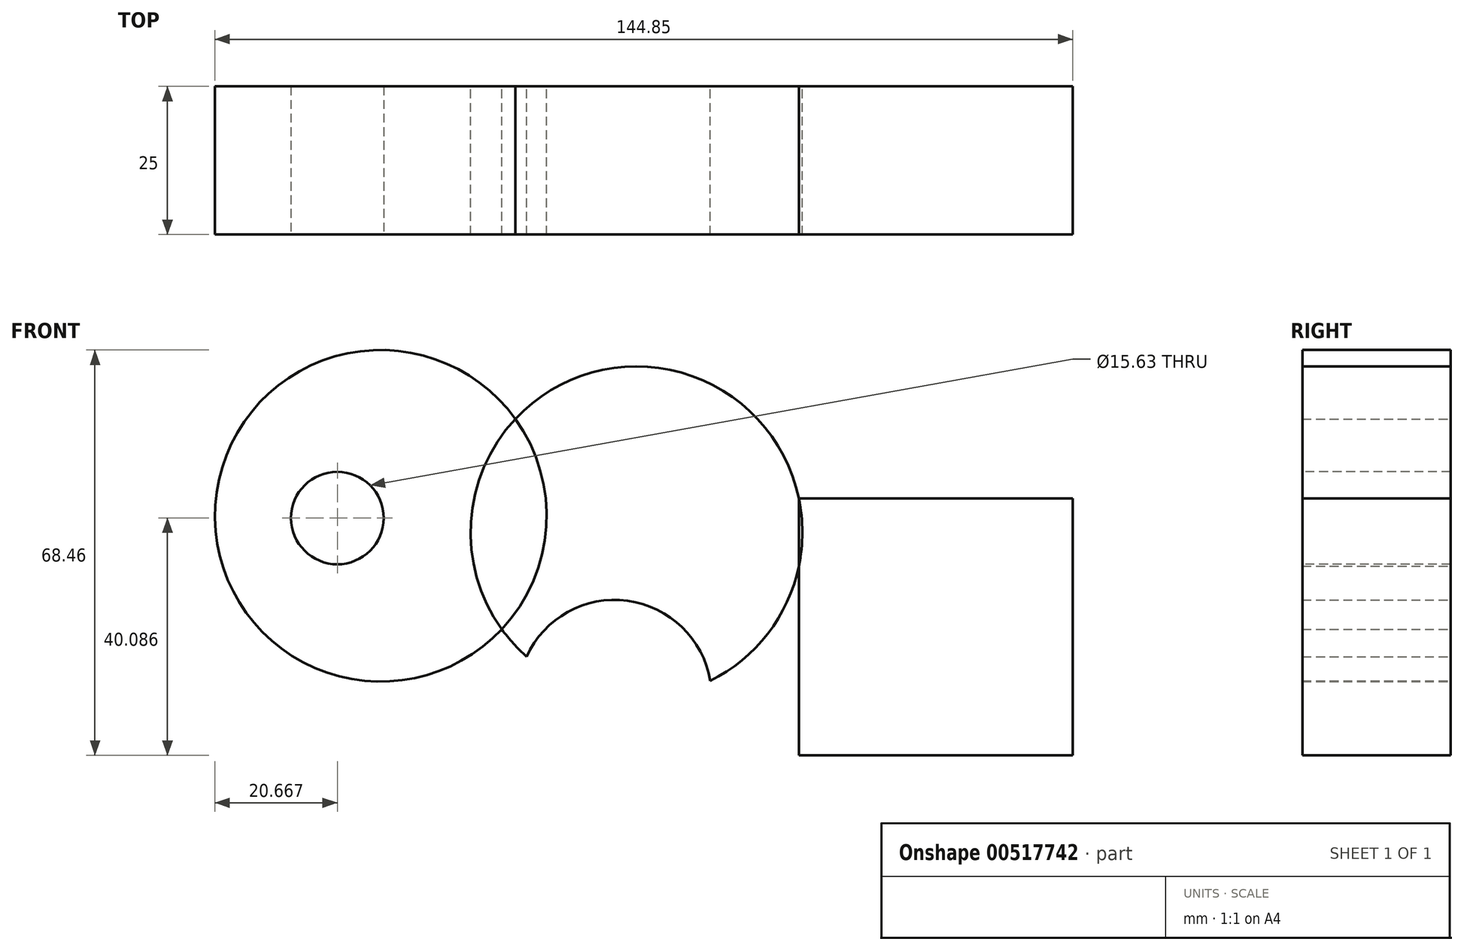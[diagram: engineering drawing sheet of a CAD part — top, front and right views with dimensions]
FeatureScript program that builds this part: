
annotation { "Feature Type Name" : "Feature", "Feature Type Description" : "" }
export const myFeature = defineFeature(function(context is Context, id is Id, definition is map)
    precondition{}
    {
        {
            var Q0;
            Q0=qCreatedBy(makeId("Front.planeOp"),FACE);
            var sketch = newSketch(context, id + "F0", { "sketchPlane" : qUnion([Q0])});
            skCircle(sketch, "E0", {"center": v(-55.9, 27.73) * mm, "radius": 28 * mm});
            skCircle(sketch, "E1", {"center": v(-12.73, 24.94) * mm, "radius": 28.01 * mm});
            skCircle(sketch, "E2", {"center": v(-16.4, -2.83) * mm, "radius": 16.36 * mm});
            skLineSegment(sketch, "E3.bottom", {"start": v(14.7, 30.64) * mm, "end": v(60.95, 30.64) * mm});
            skLineSegment(sketch, "E3.top", {"start": v(14.7, -12.73) * mm, "end": v(60.95, -12.73) * mm});
            skLineSegment(sketch, "E3.left", {"start": v(14.7, 30.64) * mm, "end": v(14.7, -12.73) * mm});
            skLineSegment(sketch, "E3.right", {"start": v(60.95, 30.64) * mm, "end": v(60.95, -12.73) * mm});
            skSolve(sketch);
        }
        {
            var Q0;
            {var subQ0=sQuery(id+"F0.wireOp",EDGE,"E1");var subQ1=sQuery(id+"F0.wireOp",EDGE,"E0");var subQ2=makeQuery(id+"F0.imprint","INTERSECT",VERTEX,{"disambiguationData":[OD(0.0)],"derivedFrom":[subQ1,subQ0]});Q0=makeQuery(id+"F0.imprint","IMPRINT",FACE,{"disambiguationData":[TD([[makeQuery(id+"F0.imprint","IMPRINT",EDGE,{"disambiguationData":[TD([[subQ2,-1.0]])],"derivedFrom":subQ1}),1.0]])]});}
            var Q1;
            {var subQ0=sQuery(id+"F0.wireOp",EDGE,"E1");var subQ1=sQuery(id+"F0.wireOp",EDGE,"E0");var subQ7=makeQuery(id+"F0.imprint","INTERSECT",VERTEX,{"disambiguationData":[OD(0.0)],"derivedFrom":[subQ1,subQ0]});Q1=makeQuery(id+"F0.imprint","IMPRINT",FACE,{"disambiguationData":[TD([[makeQuery(id+"F0.imprint","IMPRINT",EDGE,{"disambiguationData":[TD([[subQ7,1.0]])],"derivedFrom":subQ1}),-1.0]])]});}
            var Q2;
            {var subQ0=sQuery(id+"F0.wireOp",EDGE,"E2");var subQ1=sQuery(id+"F0.wireOp",EDGE,"E1");var subQ2=makeQuery(id+"F0.imprint","INTERSECT",VERTEX,{"disambiguationData":[OD(0.0)],"derivedFrom":[subQ1,subQ0]});Q2=makeQuery(id+"F0.imprint","IMPRINT",FACE,{"disambiguationData":[TD([[makeQuery(id+"F0.imprint","IMPRINT",EDGE,{"disambiguationData":[TD([[subQ2,-1.0]])],"derivedFrom":subQ1}),-1.0]])]});}
            var Q3;
            {var subQ4=sQuery(id+"F0.wireOp",EDGE,"E3.bottom");Q3=makeQuery(id+"F0.imprint","IMPRINT",FACE,{"disambiguationData":[TD([[makeQuery(id+"F0.imprint","IMPRINT",EDGE,{"derivedFrom":subQ4}),-1.0]])]});}
            extrude(context, id + "F1", {"entities" : qUnion([Q0, Q1, Q2, Q3]), "depth" : 25 * mm, "offsetDistance" : 25 * mm});
        }
        {
            var Q0;
            Q0=makeQuery(id+"F1.opExtrude","CAP_FACE",FACE,{"disambiguationData":[OSD([sQuery(id+"F0.wireOp",EDGE,"E0"),sQuery(id+"F0.wireOp",EDGE,"E1")])],"isStart":false});
            var sketch = newSketch(context, id + "F2", { "sketchPlane" : qUnion([Q0])});
            skCircle(sketch, "E4", {"center": v(-63.23, 27.36) * mm, "radius": 7.82 * mm});
            skSolve(sketch);
        }
        {
            var Q0;
            Q0=makeQuery(id+"F2.imprint","IMPRINT",FACE,{"disambiguationData":[TD([[makeQuery(id+"F2.imprint","IMPRINT",EDGE,{"derivedFrom":sQuery(id+"F2.wireOp",EDGE,"E4")}),1.0]])]});
            extrude(context, id + "F3", {"entities" : qUnion([Q0]), "operationType" : NewBodyOperationType.REMOVE, "oppositeDirection" : true, "depth" : 25 * mm, "offsetDistance" : 25 * mm});
        }
    });
